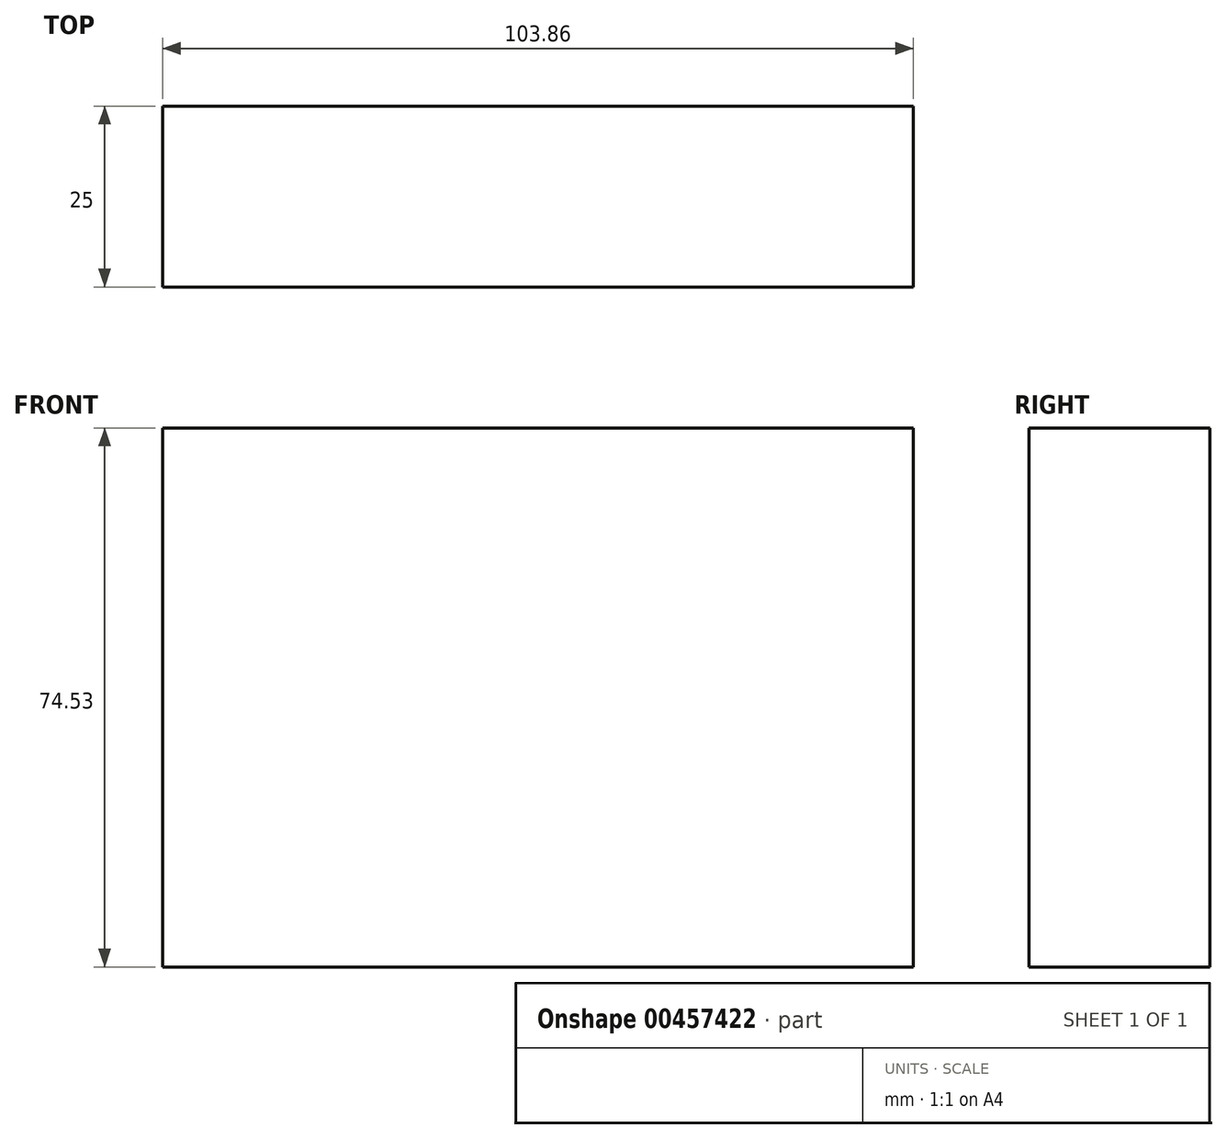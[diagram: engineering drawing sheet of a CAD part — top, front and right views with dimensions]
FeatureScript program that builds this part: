
annotation { "Feature Type Name" : "Feature", "Feature Type Description" : "" }
export const myFeature = defineFeature(function(context is Context, id is Id, definition is map)
    precondition{}
    {
        {
            var Q0;
            Q0=qCreatedBy(makeId("Front.planeOp"),FACE);
            var sketch = newSketch(context, id + "F0", { "sketchPlane" : qUnion([Q0])});
            skLineSegment(sketch, "E0.bottom", {"start": v(-68.8, 14.22) * mm, "end": v(35.06, 14.22) * mm});
            skLineSegment(sketch, "E0.top", {"start": v(-68.8, -60.3) * mm, "end": v(35.06, -60.3) * mm});
            skLineSegment(sketch, "E0.left", {"start": v(-68.8, 14.22) * mm, "end": v(-68.8, -60.3) * mm});
            skLineSegment(sketch, "E0.right", {"start": v(35.06, 14.22) * mm, "end": v(35.06, -60.3) * mm});
            skSolve(sketch);
        }
        {
            var Q0;
            Q0 = qSketchRegion(id + "F0", true);
            extrude(context, id + "F1", {"entities" : qUnion([Q0]), "depth" : 25 * mm});
        }
        {
            var Q0;
            Q0=qCreatedBy(makeId("Right.planeOp"),FACE);
            var sketch = newSketch(context, id + "F2", { "sketchPlane" : qUnion([Q0])});
            skLineSegment(sketch, "E1.bottom", {"start": v(-51.93, 37.26) * mm, "end": v(51.93, 37.26) * mm});
            skLineSegment(sketch, "E1.top", {"start": v(-51.93, -37.26) * mm, "end": v(51.93, -37.26) * mm});
            skLineSegment(sketch, "E1.left", {"start": v(-51.93, 37.26) * mm, "end": v(-51.93, -37.26) * mm});
            skLineSegment(sketch, "E1.right", {"start": v(51.93, 37.26) * mm, "end": v(51.93, -37.26) * mm});
            skSolve(sketch);
        }
        {
            var Q0;
            Q0=sQuery(id+"F2.wireOp",EDGE,"E1.bottom");
            var Q1;
            Q1=sQuery(id+"F2.wireOp",EDGE,"E1.top");
            var Q2;
            Q2=sQuery(id+"F2.wireOp",EDGE,"E1.left");
            var Q3;
            Q3=sQuery(id+"F2.wireOp",EDGE,"E1.right");
            extrude(context, id + "F3", {"bodyType" : ToolBodyType.SURFACE, "surfaceEntities" : qUnion([Q0, Q1, Q2, Q3]), "depth" : 25 * mm});
        }
    });
